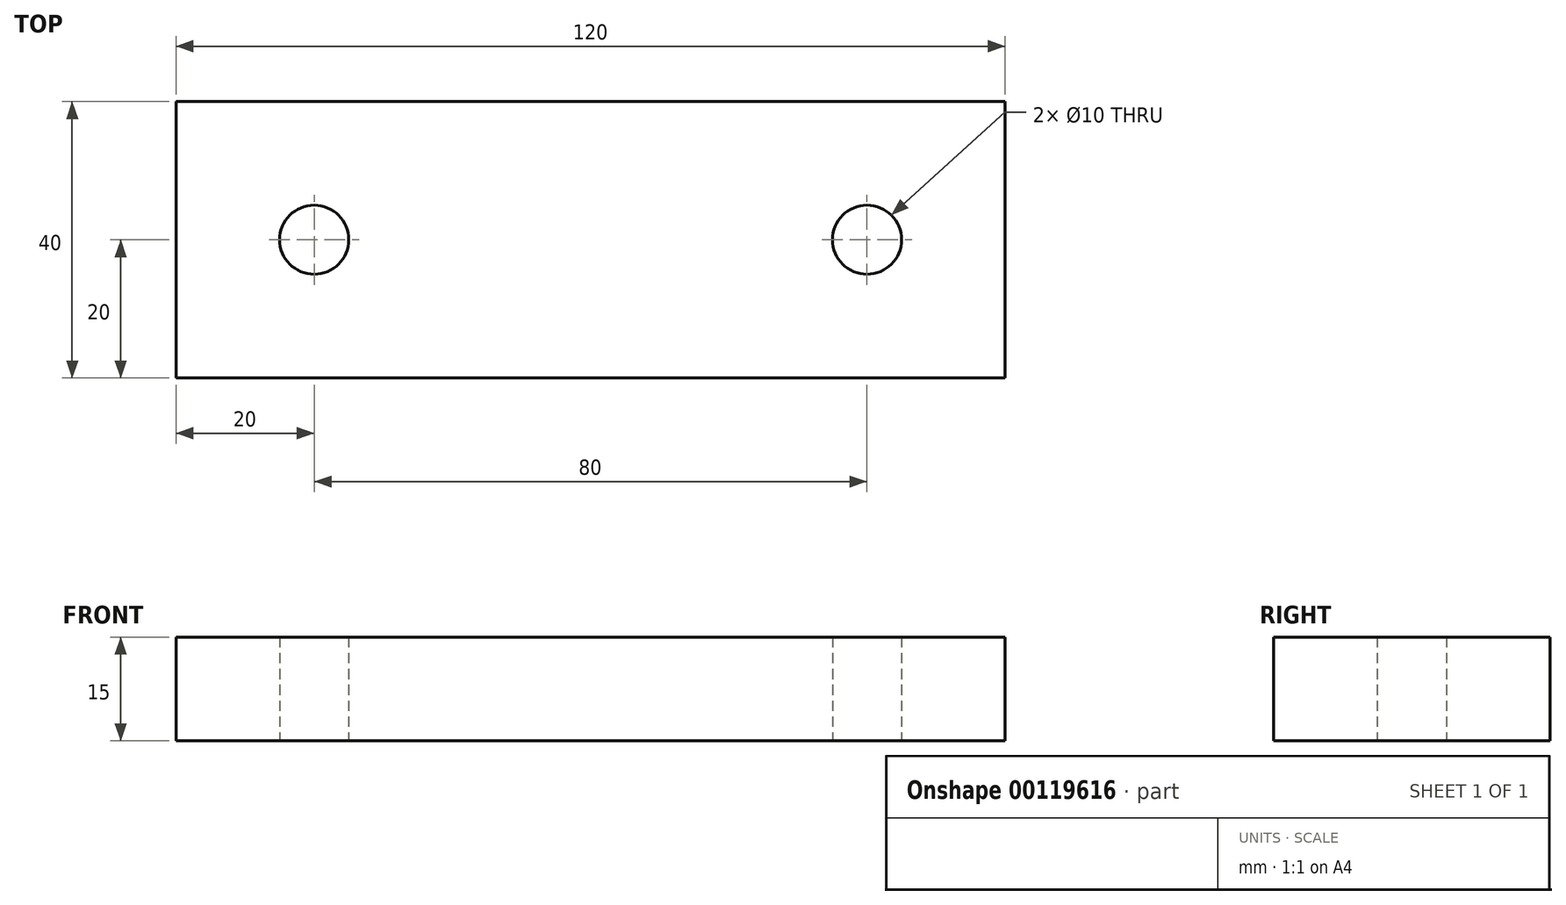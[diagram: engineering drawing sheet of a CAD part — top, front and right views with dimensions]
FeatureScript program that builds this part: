
annotation { "Feature Type Name" : "Feature", "Feature Type Description" : "" }
export const myFeature = defineFeature(function(context is Context, id is Id, definition is map)
    precondition{}
    {
        {
            var Q0;
            Q0=qCreatedBy(makeId("Top.planeOp"),FACE);
            var sketch = newSketch(context, id + "F0", { "sketchPlane" : qUnion([Q0])});
            skLineSegment(sketch, "E0.bottom", {"start": v(-60, 20) * mm, "end": v(60, 20) * mm});
            skLineSegment(sketch, "E0.top", {"start": v(-60, -20) * mm, "end": v(60, -20) * mm});
            skLineSegment(sketch, "E0.left", {"start": v(-60, 20) * mm, "end": v(-60, -20) * mm});
            skLineSegment(sketch, "E0.right", {"start": v(60, 20) * mm, "end": v(60, -20) * mm});
            skCircle(sketch, "E1", {"center": v(-40, 0) * mm, "radius": 5 * mm});
            skCircle(sketch, "E2", {"center": v(40, 0) * mm, "radius": 5 * mm});
            skSolve(sketch);
        }
        {
            var Q0;
            Q0 = qSketchRegion(id + "F0", true);
            extrude(context, id + "F1", {"entities" : qUnion([Q0]), "depth" : 15 * mm});
        }
    });
